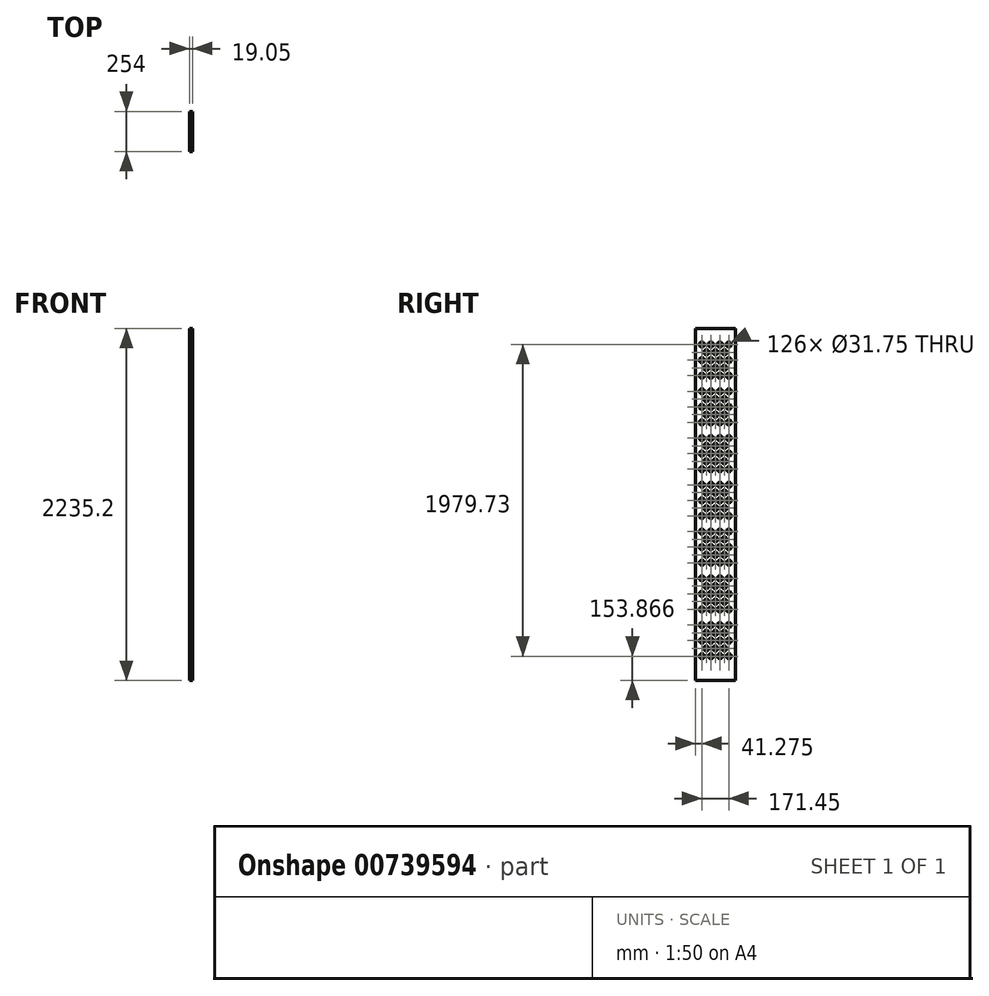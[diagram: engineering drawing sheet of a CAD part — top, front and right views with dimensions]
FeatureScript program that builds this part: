
annotation { "Feature Type Name" : "Feature", "Feature Type Description" : "" }
export const myFeature = defineFeature(function(context is Context, id is Id, definition is map)
    precondition{}
    {
        {
            var Q0;
            Q0=qCreatedBy(makeId("Right.planeOp"),FACE);
            var sketch = newSketch(context, id + "F0", { "sketchPlane" : qUnion([Q0])});
            skLineSegment(sketch, "E0.bottom", {"start": v(127, 1117.6) * mm, "end": v(-127, 1117.6) * mm, "construction": true});
            skLineSegment(sketch, "E0.top", {"start": v(127, -1117.6) * mm, "end": v(-127, -1117.6) * mm, "construction": true});
            skLineSegment(sketch, "E0.left", {"start": v(127, 1117.6) * mm, "end": v(127, -1117.6) * mm, "construction": true});
            skLineSegment(sketch, "E0.right", {"start": v(-127, 1117.6) * mm, "end": v(-127, -1117.6) * mm, "construction": true});
            skPoint(sketch, "E0.middle", {"position": v(0, 0) * mm});
            skLineSegment(sketch, "E1", {"start": v(0, 1117.6) * mm, "end": v(0, 745.07) * mm, "construction": true});
            skLineSegment(sketch, "E2", {"start": v(0, 745.07) * mm, "end": v(0, 372.53) * mm, "construction": true});
            skLineSegment(sketch, "E3", {"start": v(0, 372.53) * mm, "end": v(0, 0) * mm, "construction": true});
            skLineSegment(sketch, "E4.bottom", {"start": v(127, 735.54) * mm, "end": v(-127, 735.54) * mm});
            skLineSegment(sketch, "E4.top", {"start": v(127, 754.6) * mm, "end": v(-127, 754.6) * mm});
            skLineSegment(sketch, "E4.left", {"start": v(127, 735.54) * mm, "end": v(127, 754.6) * mm});
            skLineSegment(sketch, "E4.right", {"start": v(-127, 735.54) * mm, "end": v(-127, 754.6) * mm});
            skPoint(sketch, "E4.middle", {"position": v(0, 745.07) * mm});
            skLineSegment(sketch, "E5.bottom", {"start": v(127, 363) * mm, "end": v(-127, 363) * mm});
            skLineSegment(sketch, "E5.top", {"start": v(127, 382.06) * mm, "end": v(-127, 382.06) * mm});
            skLineSegment(sketch, "E5.left", {"start": v(127, 363) * mm, "end": v(127, 382.06) * mm});
            skLineSegment(sketch, "E5.right", {"start": v(-127, 363) * mm, "end": v(-127, 382.06) * mm});
            skPoint(sketch, "E5.middle", {"position": v(0, 372.53) * mm});
            skLineSegment(sketch, "E6.bottom", {"start": v(-127, 9.52) * mm, "end": v(127, 9.52) * mm});
            skLineSegment(sketch, "E6.top", {"start": v(-127, -9.53) * mm, "end": v(127, -9.53) * mm});
            skLineSegment(sketch, "E6.left", {"start": v(-127, 9.53) * mm, "end": v(-127, -9.53) * mm});
            skLineSegment(sketch, "E6.right", {"start": v(127, 9.52) * mm, "end": v(127, -9.52) * mm});
            skLineSegment(sketch, "E7", {"start": v(-127, 0) * mm, "end": v(127, 0) * mm, "construction": true});
            skLineSegment(sketch, "E8.MirrorCS", {"start": v(127, -382.06) * mm, "end": v(-127, -382.06) * mm});
            skLineSegment(sketch, "E9.MirrorCS", {"start": v(127, -363) * mm, "end": v(-127, -363) * mm});
            skPoint(sketch, "E10.MirrorP", {"position": v(0, -372.53) * mm});
            skLineSegment(sketch, "E11.MirrorCS", {"start": v(127, -363) * mm, "end": v(127, -382.06) * mm});
            skLineSegment(sketch, "E12.MirrorCS", {"start": v(-127, -363) * mm, "end": v(-127, -382.06) * mm});
            skLineSegment(sketch, "E13.MirrorCS", {"start": v(-127, -735.54) * mm, "end": v(-127, -754.6) * mm});
            skLineSegment(sketch, "E14.MirrorCS", {"start": v(127, -735.54) * mm, "end": v(127, -754.6) * mm});
            skPoint(sketch, "E15.MirrorP", {"position": v(0, -745.07) * mm});
            skLineSegment(sketch, "E16.MirrorCS", {"start": v(127, -754.6) * mm, "end": v(-127, -754.6) * mm});
            skLineSegment(sketch, "E17.MirrorCS", {"start": v(127, -735.54) * mm, "end": v(-127, -735.54) * mm});
            skSolve(sketch);
        }
        {
            var Q0;
            Q0=qCreatedBy(makeId("Right.planeOp"),FACE);
            var sketch = newSketch(context, id + "F1", { "sketchPlane" : qUnion([Q0])});
            skLineSegment(sketch, "E18.bottom", {"start": v(127, -1117.6) * mm, "end": v(-127, -1117.6) * mm});
            skLineSegment(sketch, "E18.top", {"start": v(127, 1117.6) * mm, "end": v(-127, 1117.6) * mm});
            skLineSegment(sketch, "E18.left", {"start": v(127, -1117.6) * mm, "end": v(127, 1117.6) * mm});
            skLineSegment(sketch, "E18.right", {"start": v(-127, -1117.6) * mm, "end": v(-127, 1117.6) * mm});
            skPoint(sketch, "E18.middle", {"position": v(0, 0) * mm});
            skLineSegment(sketch, "E19", {"start": v(-114.3, 1016) * mm, "end": v(-57.15, 1016) * mm, "construction": true});
            skLineSegment(sketch, "E20", {"start": v(-57.15, 1016) * mm, "end": v(0, 1016) * mm, "construction": true});
            skLineSegment(sketch, "E21", {"start": v(0, 1016) * mm, "end": v(57.15, 1016) * mm, "construction": true});
            skLineSegment(sketch, "E22", {"start": v(57.15, 1016) * mm, "end": v(114.3, 1016) * mm, "construction": true});
            skCircle(sketch, "E23", {"center": v(-85.72, 1016) * mm, "radius": 15.88 * mm});
            skCircle(sketch, "E24", {"center": v(-28.58, 1016) * mm, "radius": 15.88 * mm});
            skCircle(sketch, "E25", {"center": v(28.57, 1016) * mm, "radius": 15.88 * mm});
            skPoint(sketch, "E25.perimeterSnap0", {"position": v(28.57, 1016) * mm});
            skCircle(sketch, "E26", {"center": v(85.72, 1016) * mm, "radius": 15.88 * mm});
            skLineSegment(sketch, "E27", {"start": v(-114.3, 1016) * mm, "end": v(-127, 1016) * mm, "construction": true});
            skLineSegment(sketch, "E28", {"start": v(114.3, 1016) * mm, "end": v(127, 1016) * mm, "construction": true});
            skLineSegment(sketch, "E29", {"start": v(-114.3, 1086.11) * mm, "end": v(-101.6, 1086.11) * mm, "construction": true});
            skLineSegment(sketch, "E30", {"start": v(-101.6, 1016) * mm, "end": v(-101.6, 1086.11) * mm, "construction": true});
            skLineSegment(sketch, "E31", {"start": v(-114.3, 1016) * mm, "end": v(-114.3, 1086.11) * mm, "construction": true});
            skLineSegment(sketch, "E32", {"start": v(-127, 1117.6) * mm, "end": v(-85.72, 1016) * mm, "construction": true});
            skCircle(sketch, "E33", {"center": v(-57.15, 966.5) * mm, "radius": 15.88 * mm});
            skLineSegment(sketch, "E34", {"start": v(-28.58, 1016) * mm, "end": v(-57.15, 966.5) * mm, "construction": true});
            skLineSegment(sketch, "E35", {"start": v(-28.58, 1016) * mm, "end": v(-28.58, 1117.6) * mm, "construction": true});
            skPoint(sketch, "E35.endSnap0", {"position": v(0, 1117.6) * mm});
            skLineSegment(sketch, "E36", {"start": v(28.57, 1016) * mm, "end": v(28.57, 1117.6) * mm, "construction": true});
            skCircle(sketch, "E37.MirrorC", {"center": v(0, 966.5) * mm, "radius": 15.88 * mm});
            skCircle(sketch, "E38.MirrorC", {"center": v(57.15, 966.5) * mm, "radius": 15.88 * mm});
            skLineSegment(sketch, "E39", {"start": v(-57.15, 966.5) * mm, "end": v(127, 966.5) * mm, "construction": true});
            skLineSegment(sketch, "E40.direction1", {"start": v(-85.72, 1016) * mm, "end": v(-64.13, 1016) * mm, "construction": true});
            skCircle(sketch, "E41.0.1.0", {"center": v(-85.72, 917.01) * mm, "radius": 15.88 * mm});
            skCircle(sketch, "E41.0.1.1", {"center": v(-28.58, 917.01) * mm, "radius": 15.88 * mm});
            skCircle(sketch, "E41.0.1.2", {"center": v(28.57, 917.01) * mm, "radius": 15.88 * mm});
            skCircle(sketch, "E41.0.1.3", {"center": v(85.72, 917.01) * mm, "radius": 15.88 * mm});
            skCircle(sketch, "E41.0.1.4", {"center": v(57.15, 867.52) * mm, "radius": 15.88 * mm});
            skCircle(sketch, "E41.0.1.5", {"center": v(0, 867.52) * mm, "radius": 15.88 * mm});
            skCircle(sketch, "E41.0.1.6", {"center": v(-57.15, 867.52) * mm, "radius": 15.88 * mm});
            skCircle(sketch, "E41.0.2.0", {"center": v(-85.72, 818.03) * mm, "radius": 15.88 * mm});
            skCircle(sketch, "E41.0.2.1", {"center": v(-28.58, 818.03) * mm, "radius": 15.88 * mm});
            skCircle(sketch, "E41.0.2.2", {"center": v(28.57, 818.03) * mm, "radius": 15.88 * mm});
            skCircle(sketch, "E41.0.2.3", {"center": v(85.72, 818.03) * mm, "radius": 15.88 * mm});
            skCircle(sketch, "E41.0.3.0", {"center": v(-85.72, 719.04) * mm, "radius": 15.88 * mm});
            skCircle(sketch, "E41.0.3.1", {"center": v(-28.58, 719.04) * mm, "radius": 15.88 * mm});
            skCircle(sketch, "E41.0.3.2", {"center": v(28.57, 719.04) * mm, "radius": 15.88 * mm});
            skCircle(sketch, "E41.0.3.3", {"center": v(85.72, 719.04) * mm, "radius": 15.88 * mm});
            skCircle(sketch, "E41.0.3.4", {"center": v(57.15, 669.55) * mm, "radius": 15.88 * mm});
            skCircle(sketch, "E41.0.3.5", {"center": v(0, 669.55) * mm, "radius": 15.88 * mm});
            skCircle(sketch, "E41.0.3.6", {"center": v(-57.15, 669.55) * mm, "radius": 15.88 * mm});
            skCircle(sketch, "E41.0.4.0", {"center": v(-85.72, 620.05) * mm, "radius": 15.88 * mm});
            skCircle(sketch, "E41.0.4.1", {"center": v(-28.58, 620.05) * mm, "radius": 15.88 * mm});
            skCircle(sketch, "E41.0.4.2", {"center": v(28.57, 620.05) * mm, "radius": 15.88 * mm});
            skCircle(sketch, "E41.0.4.3", {"center": v(85.72, 620.05) * mm, "radius": 15.88 * mm});
            skCircle(sketch, "E41.0.4.4", {"center": v(57.15, 570.56) * mm, "radius": 15.88 * mm});
            skCircle(sketch, "E41.0.4.5", {"center": v(0, 570.56) * mm, "radius": 15.88 * mm});
            skCircle(sketch, "E41.0.4.6", {"center": v(-57.15, 570.56) * mm, "radius": 15.88 * mm});
            skCircle(sketch, "E41.0.5.0", {"center": v(-85.72, 521.07) * mm, "radius": 15.88 * mm});
            skCircle(sketch, "E41.0.5.1", {"center": v(-28.58, 521.07) * mm, "radius": 15.88 * mm});
            skCircle(sketch, "E41.0.5.2", {"center": v(28.57, 521.07) * mm, "radius": 15.88 * mm});
            skCircle(sketch, "E41.0.5.3", {"center": v(85.72, 521.07) * mm, "radius": 15.88 * mm});
            skCircle(sketch, "E41.0.6.0", {"center": v(-85.72, 422.08) * mm, "radius": 15.88 * mm});
            skCircle(sketch, "E41.0.6.1", {"center": v(-28.58, 422.08) * mm, "radius": 15.88 * mm});
            skCircle(sketch, "E41.0.6.2", {"center": v(28.57, 422.08) * mm, "radius": 15.88 * mm});
            skCircle(sketch, "E41.0.6.3", {"center": v(85.72, 422.08) * mm, "radius": 15.88 * mm});
            skCircle(sketch, "E41.0.6.4", {"center": v(57.15, 372.59) * mm, "radius": 15.88 * mm});
            skCircle(sketch, "E41.0.6.5", {"center": v(0, 372.59) * mm, "radius": 15.88 * mm});
            skCircle(sketch, "E41.0.6.6", {"center": v(-57.15, 372.59) * mm, "radius": 15.88 * mm});
            skCircle(sketch, "E41.0.7.0", {"center": v(-85.72, 323.1) * mm, "radius": 15.88 * mm});
            skCircle(sketch, "E41.0.7.1", {"center": v(-28.58, 323.1) * mm, "radius": 15.88 * mm});
            skCircle(sketch, "E41.0.7.2", {"center": v(28.57, 323.1) * mm, "radius": 15.88 * mm});
            skCircle(sketch, "E41.0.7.3", {"center": v(85.72, 323.1) * mm, "radius": 15.88 * mm});
            skCircle(sketch, "E41.0.7.4", {"center": v(57.15, 273.6) * mm, "radius": 15.88 * mm});
            skCircle(sketch, "E41.0.7.5", {"center": v(0, 273.6) * mm, "radius": 15.88 * mm});
            skCircle(sketch, "E41.0.7.6", {"center": v(-57.15, 273.6) * mm, "radius": 15.88 * mm});
            skCircle(sketch, "E41.0.8.0", {"center": v(-85.72, 224.1) * mm, "radius": 15.88 * mm});
            skCircle(sketch, "E41.0.8.1", {"center": v(-28.58, 224.1) * mm, "radius": 15.88 * mm});
            skCircle(sketch, "E41.0.8.2", {"center": v(28.57, 224.1) * mm, "radius": 15.88 * mm});
            skCircle(sketch, "E41.0.8.3", {"center": v(85.72, 224.1) * mm, "radius": 15.88 * mm});
            skCircle(sketch, "E41.0.9.0", {"center": v(-85.72, 125.12) * mm, "radius": 15.88 * mm});
            skCircle(sketch, "E41.0.9.1", {"center": v(-28.58, 125.12) * mm, "radius": 15.88 * mm});
            skCircle(sketch, "E41.0.9.2", {"center": v(28.57, 125.12) * mm, "radius": 15.88 * mm});
            skCircle(sketch, "E41.0.9.3", {"center": v(85.72, 125.12) * mm, "radius": 15.88 * mm});
            skCircle(sketch, "E41.0.9.4", {"center": v(57.15, 75.63) * mm, "radius": 15.88 * mm});
            skCircle(sketch, "E41.0.9.5", {"center": v(0, 75.63) * mm, "radius": 15.88 * mm});
            skCircle(sketch, "E41.0.9.6", {"center": v(-57.15, 75.63) * mm, "radius": 15.88 * mm});
            skCircle(sketch, "E41.0.10.0", {"center": v(-85.72, 26.13) * mm, "radius": 15.88 * mm});
            skCircle(sketch, "E41.0.10.1", {"center": v(-28.58, 26.13) * mm, "radius": 15.88 * mm});
            skCircle(sketch, "E41.0.10.2", {"center": v(28.57, 26.13) * mm, "radius": 15.88 * mm});
            skCircle(sketch, "E41.0.10.3", {"center": v(85.72, 26.13) * mm, "radius": 15.88 * mm});
            skCircle(sketch, "E41.0.10.4", {"center": v(57.15, -23.36) * mm, "radius": 15.88 * mm});
            skCircle(sketch, "E41.0.10.5", {"center": v(0, -23.36) * mm, "radius": 15.88 * mm});
            skCircle(sketch, "E41.0.10.6", {"center": v(-57.15, -23.36) * mm, "radius": 15.88 * mm});
            skCircle(sketch, "E41.0.11.0", {"center": v(-85.72, -72.85) * mm, "radius": 15.88 * mm});
            skCircle(sketch, "E41.0.11.1", {"center": v(-28.58, -72.85) * mm, "radius": 15.88 * mm});
            skCircle(sketch, "E41.0.11.2", {"center": v(28.57, -72.85) * mm, "radius": 15.88 * mm});
            skCircle(sketch, "E41.0.11.3", {"center": v(85.72, -72.85) * mm, "radius": 15.88 * mm});
            skCircle(sketch, "E41.0.12.0", {"center": v(-85.72, -171.84) * mm, "radius": 15.88 * mm});
            skCircle(sketch, "E41.0.12.1", {"center": v(-28.58, -171.84) * mm, "radius": 15.88 * mm});
            skCircle(sketch, "E41.0.12.2", {"center": v(28.57, -171.84) * mm, "radius": 15.88 * mm});
            skCircle(sketch, "E41.0.12.3", {"center": v(85.72, -171.84) * mm, "radius": 15.88 * mm});
            skCircle(sketch, "E41.0.12.4", {"center": v(57.15, -221.33) * mm, "radius": 15.88 * mm});
            skCircle(sketch, "E41.0.12.5", {"center": v(0, -221.33) * mm, "radius": 15.88 * mm});
            skCircle(sketch, "E41.0.12.6", {"center": v(-57.15, -221.33) * mm, "radius": 15.88 * mm});
            skCircle(sketch, "E41.0.13.0", {"center": v(-85.72, -270.83) * mm, "radius": 15.88 * mm});
            skCircle(sketch, "E41.0.13.1", {"center": v(-28.58, -270.83) * mm, "radius": 15.88 * mm});
            skCircle(sketch, "E41.0.13.2", {"center": v(28.57, -270.83) * mm, "radius": 15.88 * mm});
            skCircle(sketch, "E41.0.13.3", {"center": v(85.72, -270.83) * mm, "radius": 15.88 * mm});
            skCircle(sketch, "E41.0.13.4", {"center": v(57.15, -320.32) * mm, "radius": 15.88 * mm});
            skCircle(sketch, "E41.0.13.5", {"center": v(0, -320.32) * mm, "radius": 15.88 * mm});
            skCircle(sketch, "E41.0.13.6", {"center": v(-57.15, -320.32) * mm, "radius": 15.88 * mm});
            skCircle(sketch, "E41.0.14.0", {"center": v(-85.72, -369.81) * mm, "radius": 15.88 * mm});
            skCircle(sketch, "E41.0.14.1", {"center": v(-28.58, -369.81) * mm, "radius": 15.88 * mm});
            skCircle(sketch, "E41.0.14.2", {"center": v(28.57, -369.81) * mm, "radius": 15.88 * mm});
            skCircle(sketch, "E41.0.14.3", {"center": v(85.72, -369.81) * mm, "radius": 15.88 * mm});
            skCircle(sketch, "E41.0.15.0", {"center": v(-85.72, -468.8) * mm, "radius": 15.88 * mm});
            skCircle(sketch, "E41.0.15.1", {"center": v(-28.58, -468.8) * mm, "radius": 15.88 * mm});
            skCircle(sketch, "E41.0.15.2", {"center": v(28.57, -468.8) * mm, "radius": 15.88 * mm});
            skCircle(sketch, "E41.0.15.3", {"center": v(85.72, -468.8) * mm, "radius": 15.88 * mm});
            skCircle(sketch, "E41.0.15.4", {"center": v(57.15, -518.3) * mm, "radius": 15.88 * mm});
            skCircle(sketch, "E41.0.15.5", {"center": v(0, -518.3) * mm, "radius": 15.88 * mm});
            skCircle(sketch, "E41.0.15.6", {"center": v(-57.15, -518.3) * mm, "radius": 15.88 * mm});
            skCircle(sketch, "E41.0.16.0", {"center": v(-85.72, -567.79) * mm, "radius": 15.88 * mm});
            skCircle(sketch, "E41.0.16.1", {"center": v(-28.58, -567.79) * mm, "radius": 15.88 * mm});
            skCircle(sketch, "E41.0.16.2", {"center": v(28.57, -567.79) * mm, "radius": 15.88 * mm});
            skCircle(sketch, "E41.0.16.3", {"center": v(85.72, -567.79) * mm, "radius": 15.88 * mm});
            skCircle(sketch, "E41.0.16.4", {"center": v(57.15, -617.28) * mm, "radius": 15.88 * mm});
            skCircle(sketch, "E41.0.16.5", {"center": v(0, -617.28) * mm, "radius": 15.88 * mm});
            skCircle(sketch, "E41.0.16.6", {"center": v(-57.15, -617.28) * mm, "radius": 15.88 * mm});
            skCircle(sketch, "E41.0.17.0", {"center": v(-85.72, -666.77) * mm, "radius": 15.88 * mm});
            skCircle(sketch, "E41.0.17.1", {"center": v(-28.58, -666.77) * mm, "radius": 15.88 * mm});
            skCircle(sketch, "E41.0.17.2", {"center": v(28.57, -666.77) * mm, "radius": 15.88 * mm});
            skCircle(sketch, "E41.0.17.3", {"center": v(85.72, -666.77) * mm, "radius": 15.88 * mm});
            skCircle(sketch, "E41.0.18.0", {"center": v(-85.72, -765.76) * mm, "radius": 15.88 * mm});
            skCircle(sketch, "E41.0.18.1", {"center": v(-28.58, -765.76) * mm, "radius": 15.88 * mm});
            skCircle(sketch, "E41.0.18.2", {"center": v(28.57, -765.76) * mm, "radius": 15.88 * mm});
            skCircle(sketch, "E41.0.18.3", {"center": v(85.72, -765.76) * mm, "radius": 15.88 * mm});
            skCircle(sketch, "E41.0.18.4", {"center": v(57.15, -815.25) * mm, "radius": 15.88 * mm});
            skCircle(sketch, "E41.0.18.5", {"center": v(0, -815.25) * mm, "radius": 15.88 * mm});
            skCircle(sketch, "E41.0.18.6", {"center": v(-57.15, -815.25) * mm, "radius": 15.88 * mm});
            skCircle(sketch, "E41.0.19.0", {"center": v(-85.72, -864.75) * mm, "radius": 15.88 * mm});
            skCircle(sketch, "E41.0.19.1", {"center": v(-28.58, -864.75) * mm, "radius": 15.88 * mm});
            skCircle(sketch, "E41.0.19.2", {"center": v(28.57, -864.75) * mm, "radius": 15.88 * mm});
            skCircle(sketch, "E41.0.19.3", {"center": v(85.72, -864.75) * mm, "radius": 15.88 * mm});
            skCircle(sketch, "E41.0.19.4", {"center": v(57.15, -914.24) * mm, "radius": 15.88 * mm});
            skCircle(sketch, "E41.0.19.5", {"center": v(0, -914.24) * mm, "radius": 15.88 * mm});
            skCircle(sketch, "E41.0.19.6", {"center": v(-57.15, -914.24) * mm, "radius": 15.88 * mm});
            skLineSegment(sketch, "E41.direction1", {"start": v(-85.72, 1016) * mm, "end": v(-60.32, 1016) * mm, "construction": true});
            skLineSegment(sketch, "E41.direction2", {"start": v(-85.73, 1016) * mm, "end": v(-85.73, 917.01) * mm, "construction": true});
            skLineSegment(sketch, "E42.MirrorCS", {"start": v(57.15, 917.01) * mm, "end": v(114.3, 917.01) * mm, "construction": true});
            skCircle(sketch, "E43.0.0.20", {"center": v(-85.72, -963.73) * mm, "radius": 15.88 * mm});
            skCircle(sketch, "E43.2.0.20", {"center": v(-28.58, -963.73) * mm, "radius": 15.88 * mm});
            skCircle(sketch, "E43.4.0.20", {"center": v(28.57, -963.73) * mm, "radius": 15.88 * mm});
            skCircle(sketch, "E43.6.0.20", {"center": v(85.72, -963.73) * mm, "radius": 15.88 * mm});
            skSolve(sketch);
        }
        {
            var Q0;
            Q0 = qSketchRegion(id + "F1", true);
            extrude(context, id + "F2", {"entities" : qUnion([Q0]), "depth" : 19.05 * mm, "offsetDistance" : 25.4 * mm});
        }
    });
